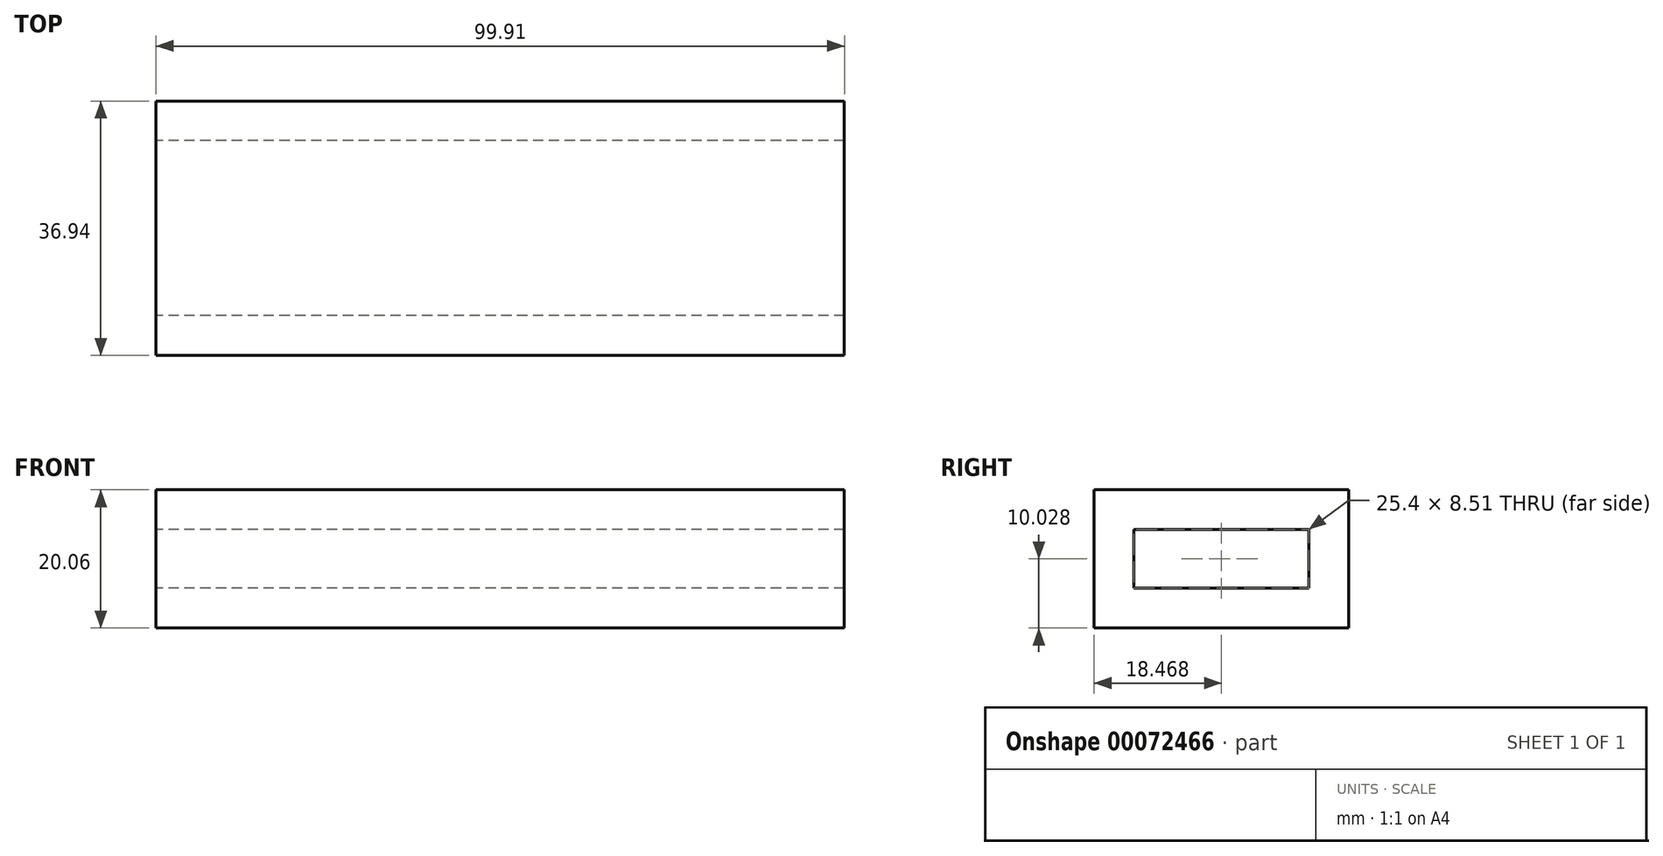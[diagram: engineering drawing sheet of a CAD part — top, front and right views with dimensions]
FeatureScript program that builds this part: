
annotation { "Feature Type Name" : "Feature", "Feature Type Description" : "" }
export const myFeature = defineFeature(function(context is Context, id is Id, definition is map)
    precondition{}
    {
        {
            var Q0;
            Q0=qCreatedBy(makeId("Top.planeOp"),FACE);
            var sketch = newSketch(context, id + "F0", { "sketchPlane" : qUnion([Q0])});
            skLineSegment(sketch, "E0.bottom", {"start": v(-50.65, 47.37) * mm, "end": v(49.26, 47.37) * mm});
            skLineSegment(sketch, "E0.top", {"start": v(-50.65, 10.43) * mm, "end": v(49.26, 10.43) * mm});
            skLineSegment(sketch, "E0.left", {"start": v(-50.65, 47.37) * mm, "end": v(-50.65, 10.43) * mm});
            skLineSegment(sketch, "E0.right", {"start": v(49.26, 47.37) * mm, "end": v(49.26, 10.43) * mm});
            skSolve(sketch);
        }
        {
            var Q0;
            Q0=makeQuery(id+"F0.imprint","IMPRINT",FACE,{"disambiguationData":[TD([[makeQuery(id+"F0.imprint","IMPRINT",EDGE,{"derivedFrom":sQuery(id+"F0.wireOp",EDGE,"E0.bottom")}),-1.0]])]});
            extrude(context, id + "F1", {"entities" : qUnion([Q0]), "depth" : 20.06 * mm});
        }
        {
            var Q0;
            Q0=makeQuery(id+"F1.opExtrude","SWEPT_FACE",FACE,{"disambiguationData":[OSD([sQuery(id+"F0.wireOp",EDGE,"E0.left")])]});
            var sketch = newSketch(context, id + "F2", { "sketchPlane" : qUnion([Q0])});
            skLineSegment(sketch, "E1.0", {"start": v(-41.6, 5.77) * mm, "end": v(-16.2, 5.77) * mm});
            skLineSegment(sketch, "E1.1", {"start": v(-41.6, 14.28) * mm, "end": v(-41.6, 5.77) * mm});
            skLineSegment(sketch, "E1.2", {"start": v(-16.2, 14.28) * mm, "end": v(-41.6, 14.28) * mm});
            skLineSegment(sketch, "E1.3", {"start": v(-16.2, 5.77) * mm, "end": v(-16.2, 14.28) * mm});
            skSolve(sketch);
        }
        {
            var Q0;
            Q0=makeQuery(id+"F2.imprint","IMPRINT",FACE,{"disambiguationData":[TD([[makeQuery(id+"F2.imprint","IMPRINT",EDGE,{"derivedFrom":sQuery(id+"F2.wireOp",EDGE,"E1.0")}),1.0]])]});
            extrude(context, id + "F3", {"entities" : qUnion([Q0]), "operationType" : NewBodyOperationType.REMOVE, "endBound" : BoundingType.THROUGH_ALL, "oppositeDirection" : true, "depth" : 25 * mm});
        }
    });
